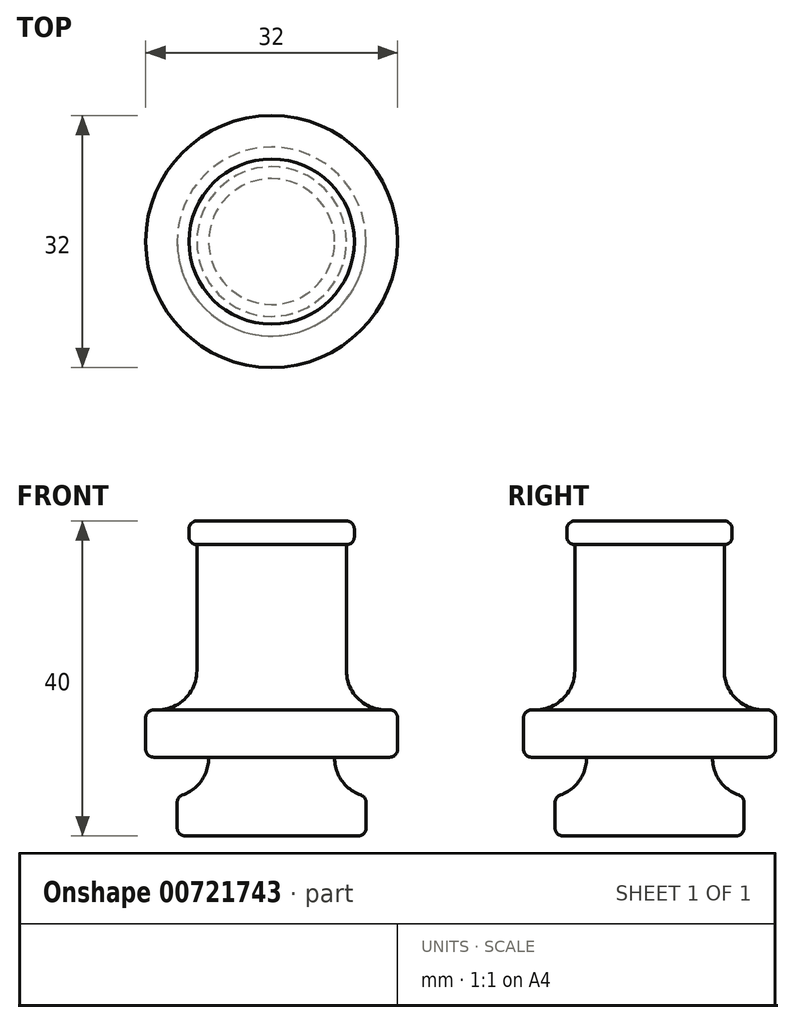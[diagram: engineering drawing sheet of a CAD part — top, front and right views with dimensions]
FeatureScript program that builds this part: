
annotation { "Feature Type Name" : "Feature", "Feature Type Description" : "" }
export const myFeature = defineFeature(function(context is Context, id is Id, definition is map)
    precondition{}
    {
        {
            var Q0;
            Q0=qCreatedBy(makeId("Right.planeOp"),FACE);
            var sketch = newSketch(context, id + "F0", { "sketchPlane" : qUnion([Q0])});
            skLineSegment(sketch, "E0", {"start": v(0, 0) * mm, "end": v(0, 50.8) * mm, "construction": true});
            skLineSegment(sketch, "E1", {"start": v(0, 0) * mm, "end": v(-16, 0) * mm});
            skLineSegment(sketch, "E2", {"start": v(-16, 0) * mm, "end": v(-16, 6) * mm});
            skLineSegment(sketch, "E3", {"start": v(-16, 6) * mm, "end": v(-9.5, 6) * mm});
            skLineSegment(sketch, "E4", {"start": v(-9.5, 6) * mm, "end": v(-9.5, 27) * mm});
            skLineSegment(sketch, "E5", {"start": v(-9.5, 27) * mm, "end": v(-10.5, 27) * mm});
            skLineSegment(sketch, "E6", {"start": v(-10.5, 27) * mm, "end": v(-10.5, 30) * mm});
            skLineSegment(sketch, "E7", {"start": v(-10.5, 30) * mm, "end": v(0, 30) * mm});
            skLineSegment(sketch, "E8", {"start": v(0, 30) * mm, "end": v(0, 0) * mm});
            skLineSegment(sketch, "E9", {"start": v(0, 0) * mm, "end": v(0, -10) * mm});
            skLineSegment(sketch, "E10", {"start": v(0, -10) * mm, "end": v(-12, -10) * mm});
            skLineSegment(sketch, "E11", {"start": v(-12, -10) * mm, "end": v(-12, -5) * mm});
            skLineSegment(sketch, "E12", {"start": v(-12, -5) * mm, "end": v(-8, -5) * mm});
            skLineSegment(sketch, "E13", {"start": v(-8, -5) * mm, "end": v(-8, 0) * mm});
            skSolve(sketch);
        }
        {
            var Q0;
            Q0=qSketchRegion(id+"F0",true);
            var Q1;
            Q1=sQuery(id+"F0.wireOp",EDGE,"E0");
            revolve(context, id + "F1", {"surfaceOperationType" : NewSurfaceOperationType.NEW, "entities" : qUnion([Q0]), "axis" : qUnion([Q1]), "revolveType" : RevolveType.FULL});
        }
        {
            var Q0;
            Q0=makeQuery(id+"F1.opRevolve","SWEPT_EDGE",EDGE,{"disambiguationData":[OSD([sQuery(id+"F0.wireOp",EDGE,"E6"),sQuery(id+"F0.wireOp",EDGE,"E7")])]});
            var Q1;
            Q1=makeQuery(id+"F1.opRevolve","SWEPT_EDGE",EDGE,{"disambiguationData":[OSD([sQuery(id+"F0.wireOp",EDGE,"E5"),sQuery(id+"F0.wireOp",EDGE,"E6")])]});
            fillet(context, id + "F2", {"entities" : qUnion([Q0, Q1]), "radius" : 1 * mm, "tangentPropagation" : true, "allowEdgeOverflow" : false});
        }
        {
            var Q0;
            Q0=makeQuery(id+"F1.opRevolve","SWEPT_EDGE",EDGE,{"disambiguationData":[OSD([sQuery(id+"F0.wireOp",EDGE,"E3"),sQuery(id+"F0.wireOp",EDGE,"E4")])]});
            var Q1;
            Q1=makeQuery(id+"F1.opRevolve","SWEPT_EDGE",EDGE,{"disambiguationData":[OSD([sQuery(id+"F0.wireOp",EDGE,"E12"),sQuery(id+"F0.wireOp",EDGE,"E13")])]});
            fillet(context, id + "F3", {"entities" : qUnion([Q0, Q1]), "radius" : 5 * mm, "tangentPropagation" : true, "allowEdgeOverflow" : false});
        }
        {
            var Q0;
            Q0=makeQuery(id+"F1.opRevolve","SWEPT_EDGE",EDGE,{"disambiguationData":[OSD([sQuery(id+"F0.wireOp",EDGE,"E2"),sQuery(id+"F0.wireOp",EDGE,"E3")])]});
            var Q1;
            Q1=makeQuery(id+"F1.opRevolve","SWEPT_EDGE",EDGE,{"disambiguationData":[OSD([sQuery(id+"F0.wireOp",EDGE,"E1"),sQuery(id+"F0.wireOp",EDGE,"E2")])]});
            var Q2;
            Q2=makeQuery(id+"F3.opFillet","BLEND_EDGE",EDGE,{"blendedFrom":[makeQuery(id+"F1.opRevolve","SWEPT_EDGE",EDGE,{"disambiguationData":[OSD([sQuery(id+"F0.wireOp",EDGE,"E12"),sQuery(id+"F0.wireOp",EDGE,"E13")])]}),makeQuery(id+"F1.opRevolve","SWEPT_FACE",FACE,{"disambiguationData":[OSD([sQuery(id+"F0.wireOp",EDGE,"E11")])]})],"blendedInto":[makeQuery(id+"F1.opRevolve","SWEPT_FACE",FACE,{"disambiguationData":[OSD([sQuery(id+"F0.wireOp",EDGE,"E11")])]})]});
            var Q3;
            Q3=makeQuery(id+"F1.opRevolve","SWEPT_EDGE",EDGE,{"disambiguationData":[OSD([sQuery(id+"F0.wireOp",EDGE,"E10"),sQuery(id+"F0.wireOp",EDGE,"E11")])]});
            fillet(context, id + "F4", {"entities" : qUnion([Q0, Q1, Q2, Q3]), "radius" : 1 * mm, "tangentPropagation" : true, "allowEdgeOverflow" : false});
        }
    });
